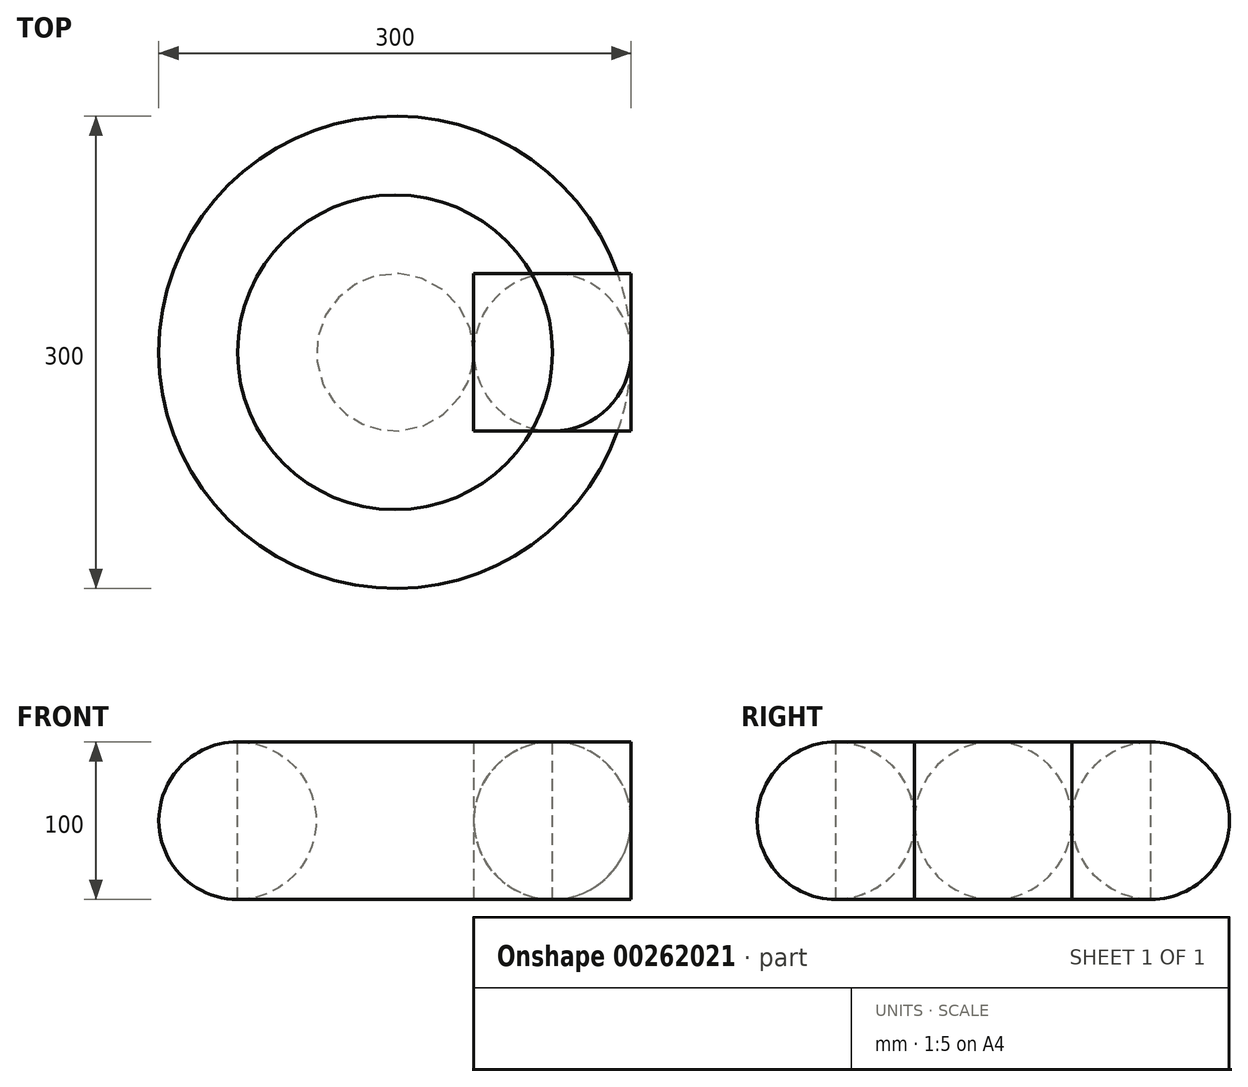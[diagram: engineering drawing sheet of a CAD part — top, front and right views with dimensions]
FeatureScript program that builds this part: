
annotation { "Feature Type Name" : "Feature", "Feature Type Description" : "" }
export const myFeature = defineFeature(function(context is Context, id is Id, definition is map)
    precondition{}
    {
        {
            var Q0;
            Q0=qCreatedBy(makeId("Front.planeOp"),FACE);
            var sketch = newSketch(context, id + "F0", { "sketchPlane" : qUnion([Q0])});
            skLineSegment(sketch, "E0.bottom", {"start": v(50, 50) * mm, "end": v(-50, 50) * mm});
            skLineSegment(sketch, "E0.top", {"start": v(50, -50) * mm, "end": v(-50, -50) * mm});
            skLineSegment(sketch, "E0.left", {"start": v(50, 50) * mm, "end": v(50, -50) * mm});
            skLineSegment(sketch, "E0.right", {"start": v(-50, 50) * mm, "end": v(-50, -50) * mm});
            skPoint(sketch, "E0.middle", {"position": v(0, 0) * mm});
            skSolve(sketch);
        }
        {
            var Q0;
            Q0=makeQuery(id+"F0.imprint","IMPRINT",FACE,{"disambiguationData":[TD([[makeQuery(id+"F0.imprint","IMPRINT",EDGE,{"derivedFrom":sQuery(id+"F0.wireOp",EDGE,"E0.bottom")}),1.0]])]});
            extrude(context, id + "F1", {"entities" : qUnion([Q0]), "depth" : 100 * mm, "offsetDistance" : 25 * mm, "symmetric" : true});
        }
        {
            var Q0;
            Q0=qCreatedBy(makeId("Front.planeOp"),FACE);
            var sketch = newSketch(context, id + "F2", { "sketchPlane" : qUnion([Q0])});
            skCircle(sketch, "E1", {"center": v(0, 0) * mm, "radius": 50 * mm});
            skLineSegment(sketch, "E2", {"start": v(0, 50) * mm, "end": v(0, -50) * mm});
            skLineSegment(sketch, "E3", {"start": v(0, 50) * mm, "end": v(-100, 50) * mm, "construction": true});
            skLineSegment(sketch, "E4", {"start": v(-100, 50) * mm, "end": v(-100, -50) * mm, "construction": true});
            skLineSegment(sketch, "E5", {"start": v(-100, -50) * mm, "end": v(0, -50) * mm, "construction": true});
            skSolve(sketch);
        }
        {
            var Q0;
            Q0=makeQuery(id+"F2.imprint","IMPRINT",FACE,{"disambiguationData":[TD([[makeQuery(id+"F2.imprint","IMPRINT",EDGE,{"derivedFrom":sQuery(id+"F2.wireOp",EDGE,"E1")}),1.0]])]});
            extrude(context, id + "F3", {"entities" : qUnion([Q0]), "depth" : 100 * mm, "offsetDistance" : 25 * mm, "symmetric" : true});
        }
        {
            var Q0;
            {var subQ0=sQuery(id+"F2.wireOp",EDGE,"E2");Q0=makeQuery(id+"F2.imprint","IMPRINT",FACE,{"disambiguationData":[TD([[makeQuery(id+"F2.imprint","IMPRINT",EDGE,{"derivedFrom":subQ0}),-1.0]])]});}
            var Q1;
            Q1=sQuery(id+"F2.wireOp",EDGE,"E2");
            revolve(context, id + "F4", {"surfaceOperationType" : NewSurfaceOperationType.NEW, "entities" : qUnion([Q0]), "axis" : qUnion([Q1]), "revolveType" : RevolveType.FULL});
        }
        {
            var Q0;
            {var subQ0=sQuery(id+"F2.wireOp",EDGE,"E2");Q0=makeQuery(id+"F2.imprint","IMPRINT",FACE,{"disambiguationData":[TD([[makeQuery(id+"F2.imprint","IMPRINT",EDGE,{"derivedFrom":subQ0}),1.0]])]});}
            var Q1;
            {var subQ0=sQuery(id+"F2.wireOp",EDGE,"E2");Q1=makeQuery(id+"F2.imprint","IMPRINT",FACE,{"disambiguationData":[TD([[makeQuery(id+"F2.imprint","IMPRINT",EDGE,{"derivedFrom":subQ0}),-1.0]])]});}
            var Q2;
            Q2=sQuery(id+"F2.wireOp",EDGE,"E4");
            revolve(context, id + "F5", {"surfaceOperationType" : NewSurfaceOperationType.NEW, "entities" : qUnion([Q0, Q1]), "axis" : qUnion([Q2]), "revolveType" : RevolveType.FULL});
        }
        {
            var Q0;
            {var subQ0=sQuery(id+"F2.wireOp",EDGE,"E2");Q0=makeQuery(id+"F2.imprint","IMPRINT",FACE,{"disambiguationData":[TD([[makeQuery(id+"F2.imprint","IMPRINT",EDGE,{"derivedFrom":subQ0}),-1.0]])]});}
            var Q1;
            Q1=sQuery(id+"F2.wireOp",EDGE,"E4");
            revolve(context, id + "F6", {"surfaceOperationType" : NewSurfaceOperationType.NEW, "entities" : qUnion([Q0]), "axis" : qUnion([Q1]), "revolveType" : RevolveType.FULL});
        }
    });
